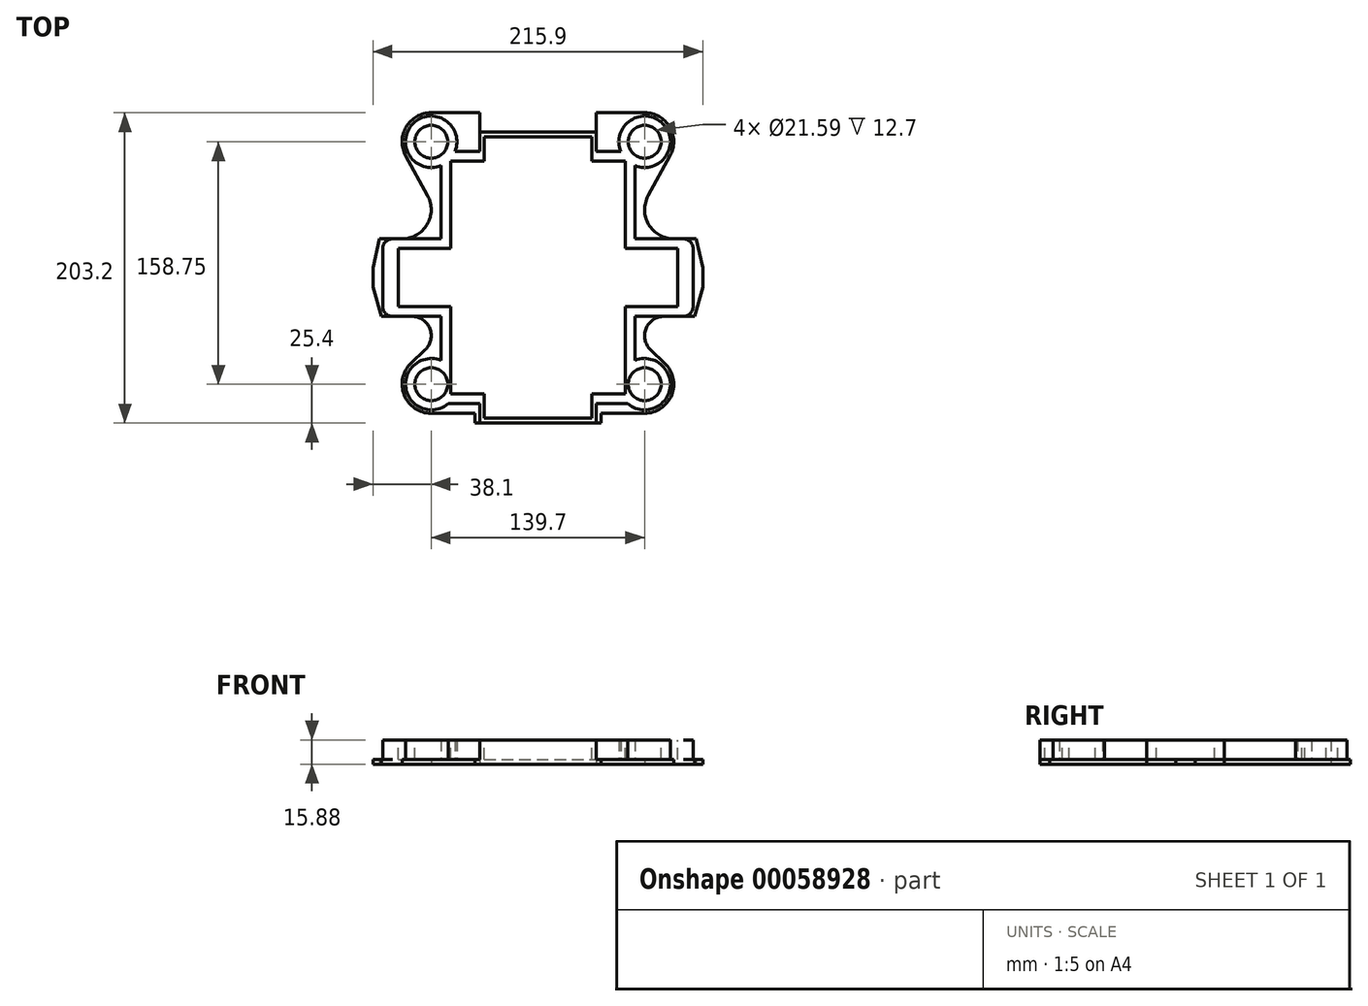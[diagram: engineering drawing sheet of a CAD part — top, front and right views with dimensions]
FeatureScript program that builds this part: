
annotation { "Feature Type Name" : "Feature", "Feature Type Description" : "" }
export const myFeature = defineFeature(function(context is Context, id is Id, definition is map)
    precondition{}
    {
        {
            var Q0;
            Q0=qCreatedBy(makeId("Top.planeOp"),FACE);
            var sketch = newSketch(context, id + "F0", { "sketchPlane" : qUnion([Q0])});
            skLineSegment(sketch, "E0", {"start": v(-107.95, 0) * mm, "end": v(107.95, 0) * mm, "construction": true});
            skLineSegment(sketch, "E1", {"start": v(0, 95.25) * mm, "end": v(0, -95.25) * mm, "construction": true});
            skArc(sketch, "E2", {"start": v(86.55, 79.73) * mm, "mid": v(86.25, 98.6) * mm, "end": v(69.85, 107.95) * mm});
            skArc(sketch, "E3", {"start": v(-69.85, 107.95) * mm, "mid": v(-86.25, 98.6) * mm, "end": v(-86.55, 79.73) * mm});
            skArc(sketch, "E4", {"start": v(69.85, -88.9) * mm, "mid": v(87.54, -76.92) * mm, "end": v(82.99, -56.06) * mm});
            skArc(sketch, "E5", {"start": v(-82.99, -56.06) * mm, "mid": v(-87.54, -76.92) * mm, "end": v(-69.85, -88.9) * mm});
            skLineSegment(sketch, "E6", {"start": v(-38.1, 95.25) * mm, "end": v(38.1, 95.25) * mm});
            skLineSegment(sketch, "E7", {"start": v(38.1, 95.25) * mm, "end": v(38.1, 107.95) * mm});
            skLineSegment(sketch, "E8", {"start": v(-38.1, 95.25) * mm, "end": v(-38.1, 107.95) * mm});
            skLineSegment(sketch, "E9", {"start": v(38.1, 107.95) * mm, "end": v(69.85, 107.95) * mm});
            skLineSegment(sketch, "E10", {"start": v(-38.1, 107.95) * mm, "end": v(-69.85, 107.95) * mm});
            skLineSegment(sketch, "E11", {"start": v(-69.85, -88.9) * mm, "end": v(-41.27, -88.9) * mm});
            skLineSegment(sketch, "E12", {"start": v(41.28, -95.25) * mm, "end": v(-41.27, -95.25) * mm});
            skLineSegment(sketch, "E13", {"start": v(-41.27, -95.25) * mm, "end": v(-41.27, -88.9) * mm});
            skLineSegment(sketch, "E14", {"start": v(41.28, -95.25) * mm, "end": v(41.28, -88.9) * mm});
            skLineSegment(sketch, "E15.trimOffspring", {"start": v(41.28, -88.9) * mm, "end": v(69.85, -88.9) * mm});
            skLineSegment(sketch, "E16", {"start": v(107.95, -6.35) * mm, "end": v(107.95, 6.35) * mm});
            skLineSegment(sketch, "E17", {"start": v(-107.95, -6.35) * mm, "end": v(-107.95, 6.35) * mm});
            skLineSegment(sketch, "E18", {"start": v(107.95, -6.35) * mm, "end": v(102.47, -25.4) * mm});
            skLineSegment(sketch, "E19", {"start": v(-107.95, -6.35) * mm, "end": v(-102.47, -25.4) * mm});
            skLineSegment(sketch, "E20", {"start": v(107.95, 6.35) * mm, "end": v(103.66, 25.4) * mm});
            skLineSegment(sketch, "E21", {"start": v(-107.95, 6.35) * mm, "end": v(-103.66, 25.4) * mm});
            skArc(sketch, "E22", {"start": v(82.55, -25.4) * mm, "mid": v(70.76, -33.38) * mm, "end": v(73.8, -47.3) * mm});
            skArc(sketch, "E23", {"start": v(-73.8, -47.3) * mm, "mid": v(-70.76, -33.38) * mm, "end": v(-82.55, -25.4) * mm});
            skLineSegment(sketch, "E24", {"start": v(82.55, -25.4) * mm, "end": v(102.47, -25.4) * mm});
            skLineSegment(sketch, "E25", {"start": v(-82.55, -25.4) * mm, "end": v(-102.47, -25.4) * mm});
            skLineSegment(sketch, "E26", {"start": v(-73.8, -47.3) * mm, "end": v(-82.99, -56.06) * mm});
            skLineSegment(sketch, "E27", {"start": v(73.8, -47.3) * mm, "end": v(82.99, -56.06) * mm});
            skArc(sketch, "E28", {"start": v(72.2, 53.62) * mm, "mid": v(72.5, 34.75) * mm, "end": v(88.9, 25.4) * mm});
            skArc(sketch, "E29", {"start": v(-88.9, 25.4) * mm, "mid": v(-72.5, 34.75) * mm, "end": v(-72.2, 53.62) * mm});
            skLineSegment(sketch, "E30", {"start": v(-88.9, 25.4) * mm, "end": v(-103.66, 25.4) * mm});
            skLineSegment(sketch, "E31", {"start": v(88.9, 25.4) * mm, "end": v(103.66, 25.4) * mm});
            skLineSegment(sketch, "E32", {"start": v(86.55, 79.73) * mm, "end": v(72.2, 53.62) * mm});
            skLineSegment(sketch, "E33", {"start": v(-86.55, 79.73) * mm, "end": v(-72.2, 53.62) * mm});
            skSolve(sketch);
        }
        {
            var Q0;
            Q0=makeQuery(id+"F0.imprint","IMPRINT",FACE,{"disambiguationData":[TD([[makeQuery(id+"F0.imprint","IMPRINT",EDGE,{"derivedFrom":sQuery(id+"F0.wireOp",EDGE,"E2")}),1.0]])]});
            extrude(context, id + "F1", {"entities" : qUnion([Q0]), "depth" : 3.17 * mm});
        }
        {
            var Q0;
            Q0=makeQuery(id+"F1.opExtrude","CAP_FACE",FACE,{"disambiguationData":[OSD([sQuery(id+"F0.wireOp",EDGE,"E2"),sQuery(id+"F0.wireOp",EDGE,"E3"),sQuery(id+"F0.wireOp",EDGE,"E4"),sQuery(id+"F0.wireOp",EDGE,"E5"),sQuery(id+"F0.wireOp",EDGE,"E6"),sQuery(id+"F0.wireOp",EDGE,"E7"),sQuery(id+"F0.wireOp",EDGE,"E8"),sQuery(id+"F0.wireOp",EDGE,"E9"),sQuery(id+"F0.wireOp",EDGE,"E10"),sQuery(id+"F0.wireOp",EDGE,"E11"),sQuery(id+"F0.wireOp",EDGE,"E12"),sQuery(id+"F0.wireOp",EDGE,"E13"),sQuery(id+"F0.wireOp",EDGE,"E14"),sQuery(id+"F0.wireOp",EDGE,"E15.trimOffspring"),sQuery(id+"F0.wireOp",EDGE,"E16"),sQuery(id+"F0.wireOp",EDGE,"E17"),sQuery(id+"F0.wireOp",EDGE,"E18"),sQuery(id+"F0.wireOp",EDGE,"E19"),sQuery(id+"F0.wireOp",EDGE,"E20"),sQuery(id+"F0.wireOp",EDGE,"E21"),sQuery(id+"F0.wireOp",EDGE,"E22"),sQuery(id+"F0.wireOp",EDGE,"E23"),sQuery(id+"F0.wireOp",EDGE,"E24"),sQuery(id+"F0.wireOp",EDGE,"E25"),sQuery(id+"F0.wireOp",EDGE,"E26"),sQuery(id+"F0.wireOp",EDGE,"E27"),sQuery(id+"F0.wireOp",EDGE,"E28"),sQuery(id+"F0.wireOp",EDGE,"E29"),sQuery(id+"F0.wireOp",EDGE,"E30"),sQuery(id+"F0.wireOp",EDGE,"E31"),sQuery(id+"F0.wireOp",EDGE,"E32"),sQuery(id+"F0.wireOp",EDGE,"E33")])],"isStart":false});
            var sketch = newSketch(context, id + "F2", { "sketchPlane" : qUnion([Q0])});
            skLineSegment(sketch, "E34.rect.bottom", {"start": v(-54.27, 82.55) * mm, "end": v(-38.1, 82.55) * mm});
            skLineSegment(sketch, "E34.rect.top", {"start": v(-58.81, -82.55) * mm, "end": v(-38.1, -82.55) * mm});
            skLineSegment(sketch, "E34.rect.left", {"start": v(-63.5, 73.32) * mm, "end": v(-63.5, 25.4) * mm});
            skLineSegment(sketch, "E34.rect.right", {"start": v(63.5, 73.32) * mm, "end": v(63.5, 25.4) * mm});
            skPoint(sketch, "E34.rect.middle", {"position": v(0, 0) * mm});
            skLineSegment(sketch, "E35.bottom", {"start": v(-38.1, 95.25) * mm, "end": v(38.1, 95.25) * mm});
            skLineSegment(sketch, "E35.top", {"start": v(-38.1, -95.25) * mm, "end": v(38.1, -95.25) * mm});
            skLineSegment(sketch, "E35.left", {"start": v(-38.1, 95.25) * mm, "end": v(-38.1, 82.55) * mm});
            skLineSegment(sketch, "E35.right", {"start": v(38.1, 95.25) * mm, "end": v(38.1, 82.55) * mm});
            skLineSegment(sketch, "E36.rect.bottom", {"start": v(95.25, -25.4) * mm, "end": v(63.5, -25.4) * mm});
            skLineSegment(sketch, "E36.rect.top", {"start": v(95.25, 25.4) * mm, "end": v(63.5, 25.4) * mm});
            skLineSegment(sketch, "E36.rect.left", {"start": v(101.6, -19.05) * mm, "end": v(101.6, 19.05) * mm});
            skLineSegment(sketch, "E36.rect.right", {"start": v(-101.6, -19.05) * mm, "end": v(-101.6, 19.05) * mm});
            skArc(sketch, "E37", {"start": v(-63.5, -54.27) * mm, "mid": v(-86.45, -72.6) * mm, "end": v(-58.81, -82.55) * mm});
            skArc(sketch, "E38", {"start": v(58.81, -82.55) * mm, "mid": v(86.45, -72.6) * mm, "end": v(63.5, -54.27) * mm});
            skArc(sketch, "E39", {"start": v(63.5, 73.32) * mm, "mid": v(81.75, 100.8) * mm, "end": v(54.27, 82.55) * mm});
            skArc(sketch, "E40", {"start": v(-54.27, 82.55) * mm, "mid": v(-81.75, 100.8) * mm, "end": v(-63.5, 73.32) * mm});
            skLineSegment(sketch, "E41.top", {"start": v(38.1, 82.55) * mm, "end": v(54.27, 82.55) * mm});
            skLineSegment(sketch, "E42.top", {"start": v(-38.1, 82.55) * mm, "end": v(-54.27, 82.55) * mm});
            skPoint(sketch, "E43.visualSharp", {"position": v(-69.85, 107.95) * mm});
            skPoint(sketch, "E44.visualSharp", {"position": v(69.85, 107.95) * mm});
            skPoint(sketch, "E45.visualSharp", {"position": v(-101.6, 25.4) * mm});
            skArc(sketch, "E45.filletArc", {"start": v(-95.25, 25.4) * mm, "mid": v(-99.74, 23.54) * mm, "end": v(-101.6, 19.05) * mm});
            skPoint(sketch, "E46.visualSharp", {"position": v(101.6, 25.4) * mm});
            skArc(sketch, "E46.filletArc", {"start": v(101.6, 19.05) * mm, "mid": v(99.74, 23.54) * mm, "end": v(95.25, 25.4) * mm});
            skPoint(sketch, "E47.visualSharp", {"position": v(101.6, -25.4) * mm});
            skArc(sketch, "E47.filletArc", {"start": v(95.25, -25.4) * mm, "mid": v(99.74, -23.54) * mm, "end": v(101.6, -19.05) * mm});
            skPoint(sketch, "E48.visualSharp", {"position": v(-101.6, -25.4) * mm});
            skArc(sketch, "E48.filletArc", {"start": v(-101.6, -19.05) * mm, "mid": v(-99.74, -23.54) * mm, "end": v(-95.25, -25.4) * mm});
            skLineSegment(sketch, "E49.trimOffspring", {"start": v(38.1, -82.55) * mm, "end": v(38.1, -95.25) * mm});
            skLineSegment(sketch, "E50.trimOffspring", {"start": v(-38.1, -82.55) * mm, "end": v(-38.1, -95.25) * mm});
            skLineSegment(sketch, "E51.trimOffspring", {"start": v(-63.5, -25.4) * mm, "end": v(-95.25, -25.4) * mm});
            skLineSegment(sketch, "E52.trimOffspring", {"start": v(38.1, -82.55) * mm, "end": v(58.81, -82.55) * mm});
            skLineSegment(sketch, "E53.trimOffspring", {"start": v(63.5, -25.4) * mm, "end": v(63.5, -54.27) * mm});
            skLineSegment(sketch, "E54.trimOffspring", {"start": v(-63.5, -25.4) * mm, "end": v(-63.5, -54.27) * mm});
            skLineSegment(sketch, "E55.trimOffspring", {"start": v(-63.5, 25.4) * mm, "end": v(-95.25, 25.4) * mm});
            skPoint(sketch, "E56.orphan", {"position": v(63.5, -82.55) * mm});
            skPoint(sketch, "E57.orphan", {"position": v(-63.5, -82.55) * mm});
            skPoint(sketch, "E58.orphan", {"position": v(-63.5, 82.55) * mm});
            skPoint(sketch, "E59.trimOffspring.start.orphan", {"position": v(63.5, 82.55) * mm});
            skPoint(sketch, "E41.right.end.orphan", {"position": v(69.85, 82.55) * mm});
            skPoint(sketch, "E42.right.end.orphan", {"position": v(-69.85, 82.55) * mm});
            skSolve(sketch);
        }
        {
            var Q0;
            Q0=makeQuery(id+"F2.imprint","IMPRINT",FACE,{"disambiguationData":[TD([[makeQuery(id+"F2.imprint","IMPRINT",EDGE,{"derivedFrom":sQuery(id+"F2.wireOp",EDGE,"E34.rect.top")}),1.0]])]});
            extrude(context, id + "F3", {"entities" : qUnion([Q0]), "operationType" : NewBodyOperationType.ADD, "depth" : 12.7 * mm});
        }
        {
            var Q0;
            Q0=makeQuery(id+"F3.opExtrude","CAP_FACE",FACE,{"disambiguationData":[OSD([sQuery(id+"F2.wireOp",EDGE,"E34.rect.top"),sQuery(id+"F2.wireOp",EDGE,"E34.rect.left"),sQuery(id+"F2.wireOp",EDGE,"E34.rect.right"),sQuery(id+"F2.wireOp",EDGE,"E35.bottom"),sQuery(id+"F2.wireOp",EDGE,"E35.top"),sQuery(id+"F2.wireOp",EDGE,"E36.rect.bottom"),sQuery(id+"F2.wireOp",EDGE,"E36.rect.top"),sQuery(id+"F2.wireOp",EDGE,"E36.rect.left"),sQuery(id+"F2.wireOp",EDGE,"E36.rect.right"),sQuery(id+"F2.wireOp",EDGE,"E37"),sQuery(id+"F2.wireOp",EDGE,"E38"),sQuery(id+"F2.wireOp",EDGE,"E39"),sQuery(id+"F2.wireOp",EDGE,"E40"),sQuery(id+"F2.wireOp",EDGE,"E35.right"),sQuery(id+"F2.wireOp",EDGE,"E42.top"),sQuery(id+"F2.wireOp",EDGE,"E35.left"),sQuery(id+"F2.wireOp",EDGE,"E45.filletArc"),sQuery(id+"F2.wireOp",EDGE,"E46.filletArc"),sQuery(id+"F2.wireOp",EDGE,"E47.filletArc"),sQuery(id+"F2.wireOp",EDGE,"E48.filletArc"),sQuery(id+"F2.wireOp",EDGE,"E49.trimOffspring"),sQuery(id+"F2.wireOp",EDGE,"E50.trimOffspring"),sQuery(id+"F2.wireOp",EDGE,"E51.trimOffspring"),sQuery(id+"F2.wireOp",EDGE,"E52.trimOffspring"),sQuery(id+"F2.wireOp",EDGE,"E53.trimOffspring"),sQuery(id+"F2.wireOp",EDGE,"E54.trimOffspring"),sQuery(id+"F2.wireOp",EDGE,"E55.trimOffspring"),sQuery(id+"F2.wireOp",EDGE,"E41.top")])],"isStart":false});
            var sketch = newSketch(context, id + "F4", { "sketchPlane" : qUnion([Q0])});
            skLineSegment(sketch, "E60.bottom", {"start": v(-57.15, 76.2) * mm, "end": v(-35.18, 76.2) * mm});
            skLineSegment(sketch, "E60.top", {"start": v(-57.15, -76.2) * mm, "end": v(-35.18, -76.2) * mm});
            skLineSegment(sketch, "E60.left", {"start": v(-57.15, 76.2) * mm, "end": v(-57.15, 19.05) * mm});
            skLineSegment(sketch, "E60.right", {"start": v(57.15, 76.2) * mm, "end": v(57.15, 19.05) * mm});
            skLineSegment(sketch, "E61.bottom", {"start": v(-91.44, 19.05) * mm, "end": v(-57.15, 19.05) * mm});
            skLineSegment(sketch, "E61.top", {"start": v(-91.44, -19.05) * mm, "end": v(-57.15, -19.05) * mm});
            skLineSegment(sketch, "E61.left", {"start": v(-91.44, 19.05) * mm, "end": v(-91.44, -19.05) * mm});
            skLineSegment(sketch, "E61.right", {"start": v(91.44, 19.05) * mm, "end": v(91.44, -19.05) * mm});
            skLineSegment(sketch, "E62.top", {"start": v(-35.18, 92.08) * mm, "end": v(35.18, 92.08) * mm});
            skLineSegment(sketch, "E62.left", {"start": v(-35.18, 76.2) * mm, "end": v(-35.18, 92.08) * mm});
            skLineSegment(sketch, "E62.right", {"start": v(35.18, 76.2) * mm, "end": v(35.18, 92.08) * mm});
            skLineSegment(sketch, "E63.top", {"start": v(-35.18, -92.08) * mm, "end": v(35.18, -92.08) * mm});
            skLineSegment(sketch, "E63.left", {"start": v(-35.18, -76.2) * mm, "end": v(-35.18, -92.08) * mm});
            skLineSegment(sketch, "E63.right", {"start": v(35.18, -76.2) * mm, "end": v(35.18, -92.08) * mm});
            skLineSegment(sketch, "E64.trimOffspring", {"start": v(35.18, 76.2) * mm, "end": v(57.15, 76.2) * mm});
            skLineSegment(sketch, "E65.trimOffspring", {"start": v(57.15, 19.05) * mm, "end": v(91.44, 19.05) * mm});
            skLineSegment(sketch, "E66.trimOffspring", {"start": v(-57.15, -19.05) * mm, "end": v(-57.15, -76.2) * mm});
            skLineSegment(sketch, "E67.trimOffspring", {"start": v(57.15, -19.05) * mm, "end": v(57.15, -76.2) * mm});
            skLineSegment(sketch, "E68.trimOffspring", {"start": v(57.15, -19.05) * mm, "end": v(91.44, -19.05) * mm});
            skLineSegment(sketch, "E69.trimOffspring", {"start": v(35.18, -76.2) * mm, "end": v(57.15, -76.2) * mm});
            skSolve(sketch);
        }
        {
            var Q0;
            Q0=makeQuery(id+"F4.imprint","IMPRINT",FACE,{"disambiguationData":[TD([[makeQuery(id+"F4.imprint","IMPRINT",EDGE,{"derivedFrom":sQuery(id+"F4.wireOp",EDGE,"E60.bottom")}),-1.0]])]});
            extrude(context, id + "F5", {"entities" : qUnion([Q0]), "operationType" : NewBodyOperationType.REMOVE, "oppositeDirection" : true, "depth" : 12.7 * mm});
        }
        {
            var Q0;
            Q0=makeQuery(id+"F3.opExtrude","CAP_FACE",FACE,{"disambiguationData":[OSD([sQuery(id+"F2.wireOp",EDGE,"E34.rect.top"),sQuery(id+"F2.wireOp",EDGE,"E34.rect.left"),sQuery(id+"F2.wireOp",EDGE,"E34.rect.right"),sQuery(id+"F2.wireOp",EDGE,"E35.bottom"),sQuery(id+"F2.wireOp",EDGE,"E35.top"),sQuery(id+"F2.wireOp",EDGE,"E36.rect.bottom"),sQuery(id+"F2.wireOp",EDGE,"E36.rect.top"),sQuery(id+"F2.wireOp",EDGE,"E36.rect.left"),sQuery(id+"F2.wireOp",EDGE,"E36.rect.right"),sQuery(id+"F2.wireOp",EDGE,"E37"),sQuery(id+"F2.wireOp",EDGE,"E38"),sQuery(id+"F2.wireOp",EDGE,"E39"),sQuery(id+"F2.wireOp",EDGE,"E40"),sQuery(id+"F2.wireOp",EDGE,"E35.right"),sQuery(id+"F2.wireOp",EDGE,"E42.top"),sQuery(id+"F2.wireOp",EDGE,"E35.left"),sQuery(id+"F2.wireOp",EDGE,"E45.filletArc"),sQuery(id+"F2.wireOp",EDGE,"E46.filletArc"),sQuery(id+"F2.wireOp",EDGE,"E47.filletArc"),sQuery(id+"F2.wireOp",EDGE,"E48.filletArc"),sQuery(id+"F2.wireOp",EDGE,"E49.trimOffspring"),sQuery(id+"F2.wireOp",EDGE,"E50.trimOffspring"),sQuery(id+"F2.wireOp",EDGE,"E51.trimOffspring"),sQuery(id+"F2.wireOp",EDGE,"E52.trimOffspring"),sQuery(id+"F2.wireOp",EDGE,"E53.trimOffspring"),sQuery(id+"F2.wireOp",EDGE,"E54.trimOffspring"),sQuery(id+"F2.wireOp",EDGE,"E55.trimOffspring"),sQuery(id+"F2.wireOp",EDGE,"E41.top")])],"isStart":false});
            var sketch = newSketch(context, id + "F6", { "sketchPlane" : qUnion([Q0])});
            skCircle(sketch, "E70", {"center": v(-69.85, -69.85) * mm, "radius": 10.8 * mm});
            skCircle(sketch, "E71", {"center": v(-69.85, 88.9) * mm, "radius": 10.8 * mm});
            skCircle(sketch, "E72", {"center": v(69.85, 88.9) * mm, "radius": 10.8 * mm});
            skCircle(sketch, "E73", {"center": v(69.85, -69.85) * mm, "radius": 10.8 * mm});
            skSolve(sketch);
        }
        {
            var Q0;
            Q0=makeQuery(id+"F6.imprint","IMPRINT",FACE,{"disambiguationData":[TD([[makeQuery(id+"F6.imprint","IMPRINT",EDGE,{"derivedFrom":sQuery(id+"F6.wireOp",EDGE,"E70")}),1.0]])]});
            var Q1;
            Q1=makeQuery(id+"F6.imprint","IMPRINT",FACE,{"disambiguationData":[TD([[makeQuery(id+"F6.imprint","IMPRINT",EDGE,{"derivedFrom":sQuery(id+"F6.wireOp",EDGE,"E71")}),1.0]])]});
            var Q2;
            Q2=makeQuery(id+"F6.imprint","IMPRINT",FACE,{"disambiguationData":[TD([[makeQuery(id+"F6.imprint","IMPRINT",EDGE,{"derivedFrom":sQuery(id+"F6.wireOp",EDGE,"E72")}),1.0]])]});
            var Q3;
            Q3=makeQuery(id+"F6.imprint","IMPRINT",FACE,{"disambiguationData":[TD([[makeQuery(id+"F6.imprint","IMPRINT",EDGE,{"derivedFrom":sQuery(id+"F6.wireOp",EDGE,"E73")}),1.0]])]});
            extrude(context, id + "F7", {"entities" : qUnion([Q0, Q1, Q2, Q3]), "operationType" : NewBodyOperationType.REMOVE, "oppositeDirection" : true, "depth" : 12.7 * mm});
        }
    });
